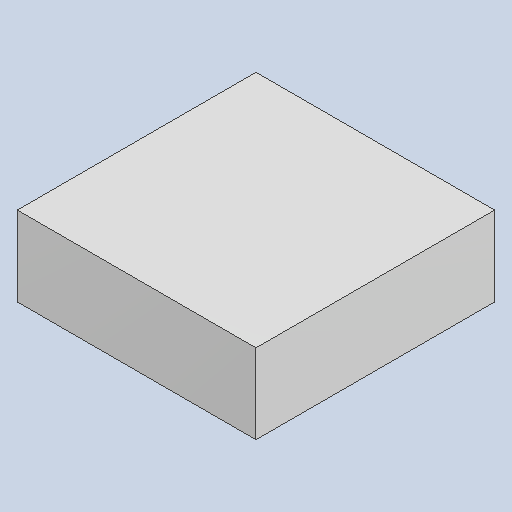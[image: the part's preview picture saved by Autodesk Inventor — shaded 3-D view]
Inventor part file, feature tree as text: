
AUTODESK INVENTOR PART (.ipt)
format: ipt  version: 2023.4 (Build 274418000, 418)  size: 79,872 bytes
history: native  units: mm
features: extrude x1
ambient origin geometry x8: Origin, YZ Plane, XZ Plane, XY Plane, X Axis, Y Axis, Z Axis, Center Point
bodies: Solid1 (feature_tree)
feature tree (1):
  extrude  "Extruded_52"  [1 undecoded]
note: 1 required parameter value undecoded (feature->parameter linkage not recoverable at this tier; creation-order binding heuristic only, values carry confidence <= 0.55)
